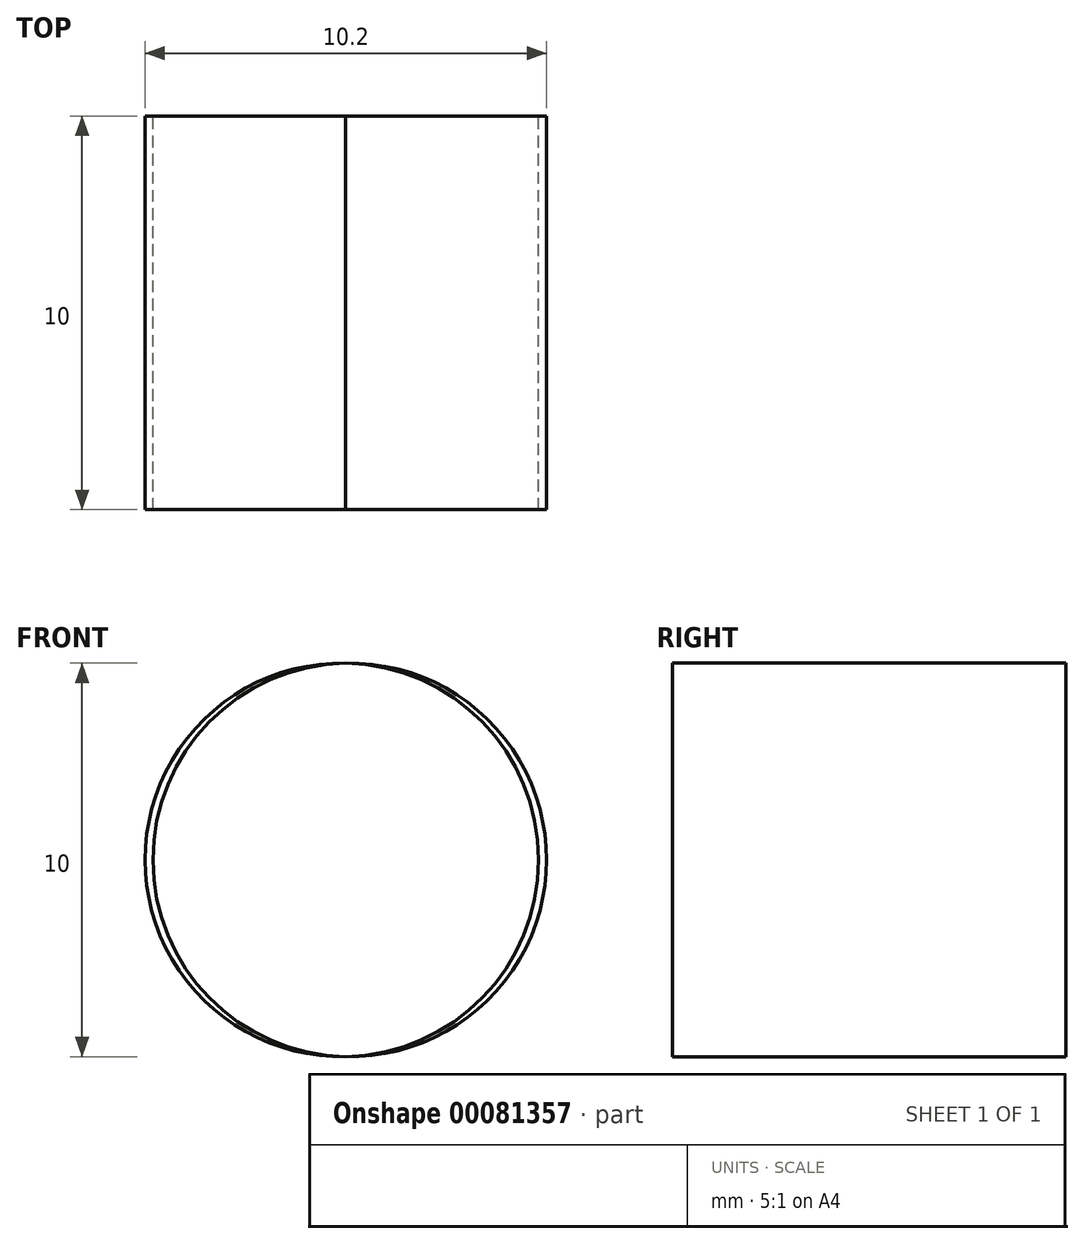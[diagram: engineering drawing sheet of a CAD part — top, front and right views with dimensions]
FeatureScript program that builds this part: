
annotation { "Feature Type Name" : "Feature", "Feature Type Description" : "" }
export const myFeature = defineFeature(function(context is Context, id is Id, definition is map)
    precondition{}
    {
        {
            var Q0;
            Q0=qCreatedBy(makeId("Front.planeOp"),FACE);
            var sketch = newSketch(context, id + "F0", { "sketchPlane" : qUnion([Q0])});
            skLineSegment(sketch, "E0", {"start": v(0, 0) * mm, "end": v(0, 40) * mm});
            skLineSegment(sketch, "E1", {"start": v(-20, 0) * mm, "end": v(-20, 40) * mm});
            skCircle(sketch, "E2", {"center": v(-10, 20) * mm, "radius": 5 * mm});
            skCircle(sketch, "E3.1.0.0", {"center": v(-10, 40) * mm, "radius": 5 * mm});
            skArc(sketch, "E4", {"start": v(15, 55) * mm, "mid": v(4.4, 50.6) * mm, "end": v(0, 40) * mm});
            skArc(sketch, "E5", {"start": v(15, 75) * mm, "mid": v(-9.75, 64.75) * mm, "end": v(-20, 40) * mm});
            skCircle(sketch, "E6.1.0", {"center": v(-2.68, 57.68) * mm, "radius": 5 * mm});
            skArc(sketch, "E6.2.0", {"start": v(15, 70) * mm, "mid": v(10, 65) * mm, "end": v(15, 60) * mm});
            skArc(sketch, "E7.1.0.0", {"start": v(-4.75, 0) * mm, "mid": v(-9.75, 5) * mm, "end": v(-14.75, 0) * mm});
            skArc(sketch, "E8.MirrorCS", {"start": v(15, 75) * mm, "mid": v(39.75, 64.75) * mm, "end": v(50, 40) * mm});
            skArc(sketch, "E9.MirrorCS", {"start": v(15, 55) * mm, "mid": v(25.6, 50.6) * mm, "end": v(30, 40) * mm});
            skLineSegment(sketch, "E10.MirrorCS", {"start": v(30, 0) * mm, "end": v(30, 40) * mm});
            skArc(sketch, "E11.MirrorCS", {"start": v(15, 69.8) * mm, "mid": v(20, 64.8) * mm, "end": v(15, 59.8) * mm});
            skLineSegment(sketch, "E12.MirrorCS", {"start": v(50, 0) * mm, "end": v(50, 40) * mm});
            skCircle(sketch, "E13.MirrorC", {"center": v(39.8, 40) * mm, "radius": 5 * mm});
            skArc(sketch, "E14.MirrorCS", {"start": v(34.75, 0) * mm, "mid": v(39.75, 5) * mm, "end": v(44.75, 0) * mm});
            skCircle(sketch, "E15.MirrorC", {"center": v(40, 40) * mm, "radius": 5 * mm});
            skCircle(sketch, "E16.MirrorC", {"center": v(32.54, 57.54) * mm, "radius": 5 * mm});
            skCircle(sketch, "E17.MirrorC", {"center": v(40, 20) * mm, "radius": 5 * mm});
            skLineSegment(sketch, "E18.MirrorCS", {"start": v(-19.8, 0) * mm, "end": v(-19.8, -40) * mm});
            skLineSegment(sketch, "E19.MirrorCS", {"start": v(0, 0) * mm, "end": v(0, -40) * mm});
            skArc(sketch, "E20.MirrorCS", {"start": v(15, -54.8) * mm, "mid": v(4.4, -50.4) * mm, "end": v(0, -39.8) * mm});
            skArc(sketch, "E21.MirrorCS", {"start": v(15, -55) * mm, "mid": v(25.6, -50.6) * mm, "end": v(30, -40) * mm});
            skArc(sketch, "E22.MirrorCS", {"start": v(14.8, -75) * mm, "mid": v(39.55, -64.75) * mm, "end": v(49.8, -40) * mm});
            skArc(sketch, "E23.MirrorCS", {"start": v(15, -75) * mm, "mid": v(-9.75, -64.75) * mm, "end": v(-20, -40) * mm});
            skLineSegment(sketch, "E24.MirrorCS", {"start": v(30, 0) * mm, "end": v(30, -40) * mm});
            skLineSegment(sketch, "E25.MirrorCS", {"start": v(50, 0) * mm, "end": v(50, -40) * mm});
            skArc(sketch, "E26.MirrorCS", {"start": v(34.75, 0) * mm, "mid": v(39.75, -5) * mm, "end": v(44.75, 0) * mm});
            skArc(sketch, "E27.MirrorCS", {"start": v(-4.75, 0) * mm, "mid": v(-9.75, -5) * mm, "end": v(-14.75, 0) * mm});
            skCircle(sketch, "E28.MirrorC", {"center": v(-10, -20) * mm, "radius": 5 * mm});
            skCircle(sketch, "E29.MirrorC", {"center": v(-9.8, -40) * mm, "radius": 5 * mm});
            skCircle(sketch, "E30.MirrorC", {"center": v(-2.54, -57.54) * mm, "radius": 5 * mm});
            skArc(sketch, "E31.MirrorCS", {"start": v(15, -69.8) * mm, "mid": v(10, -64.8) * mm, "end": v(15, -59.8) * mm});
            skArc(sketch, "E32.MirrorCS", {"start": v(15, -69.8) * mm, "mid": v(20, -64.8) * mm, "end": v(15, -59.8) * mm});
            skCircle(sketch, "E33.MirrorC", {"center": v(32.54, -57.54) * mm, "radius": 5 * mm});
            skCircle(sketch, "E34.MirrorC", {"center": v(39.8, -40) * mm, "radius": 5 * mm});
            skCircle(sketch, "E35.MirrorC", {"center": v(40, -20) * mm, "radius": 5 * mm});
            skSolve(sketch);
        }
        {
            var Q0;
            {var subQ0=sQuery(id+"F0.wireOp",EDGE,"E15.MirrorC");var subQ1=sQuery(id+"F0.wireOp",EDGE,"E13.MirrorC");var subQ2=makeQuery(id+"F0.imprint","INTERSECT",VERTEX,{"disambiguationData":[OD(0.0)],"derivedFrom":[subQ1,subQ0]});Q0=makeQuery(id+"F0.imprint","IMPRINT",FACE,{"disambiguationData":[TD([[makeQuery(id+"F0.imprint","IMPRINT",EDGE,{"disambiguationData":[TD([[subQ2,1.0]])],"derivedFrom":subQ1}),1.0]])]});}
            var Q1;
            {var subQ0=sQuery(id+"F0.wireOp",EDGE,"E15.MirrorC");var subQ1=sQuery(id+"F0.wireOp",EDGE,"E13.MirrorC");var subQ2=makeQuery(id+"F0.imprint","INTERSECT",VERTEX,{"disambiguationData":[OD(0.0)],"derivedFrom":[subQ1,subQ0]});Q1=makeQuery(id+"F0.imprint","IMPRINT",FACE,{"disambiguationData":[TD([[makeQuery(id+"F0.imprint","IMPRINT",EDGE,{"disambiguationData":[TD([[subQ2,-1.0]])],"derivedFrom":subQ1}),-1.0]])]});}
            extrude(context, id + "F1", {"entities" : qUnion([Q0, Q1]), "depth" : 10 * mm});
        }
    });
